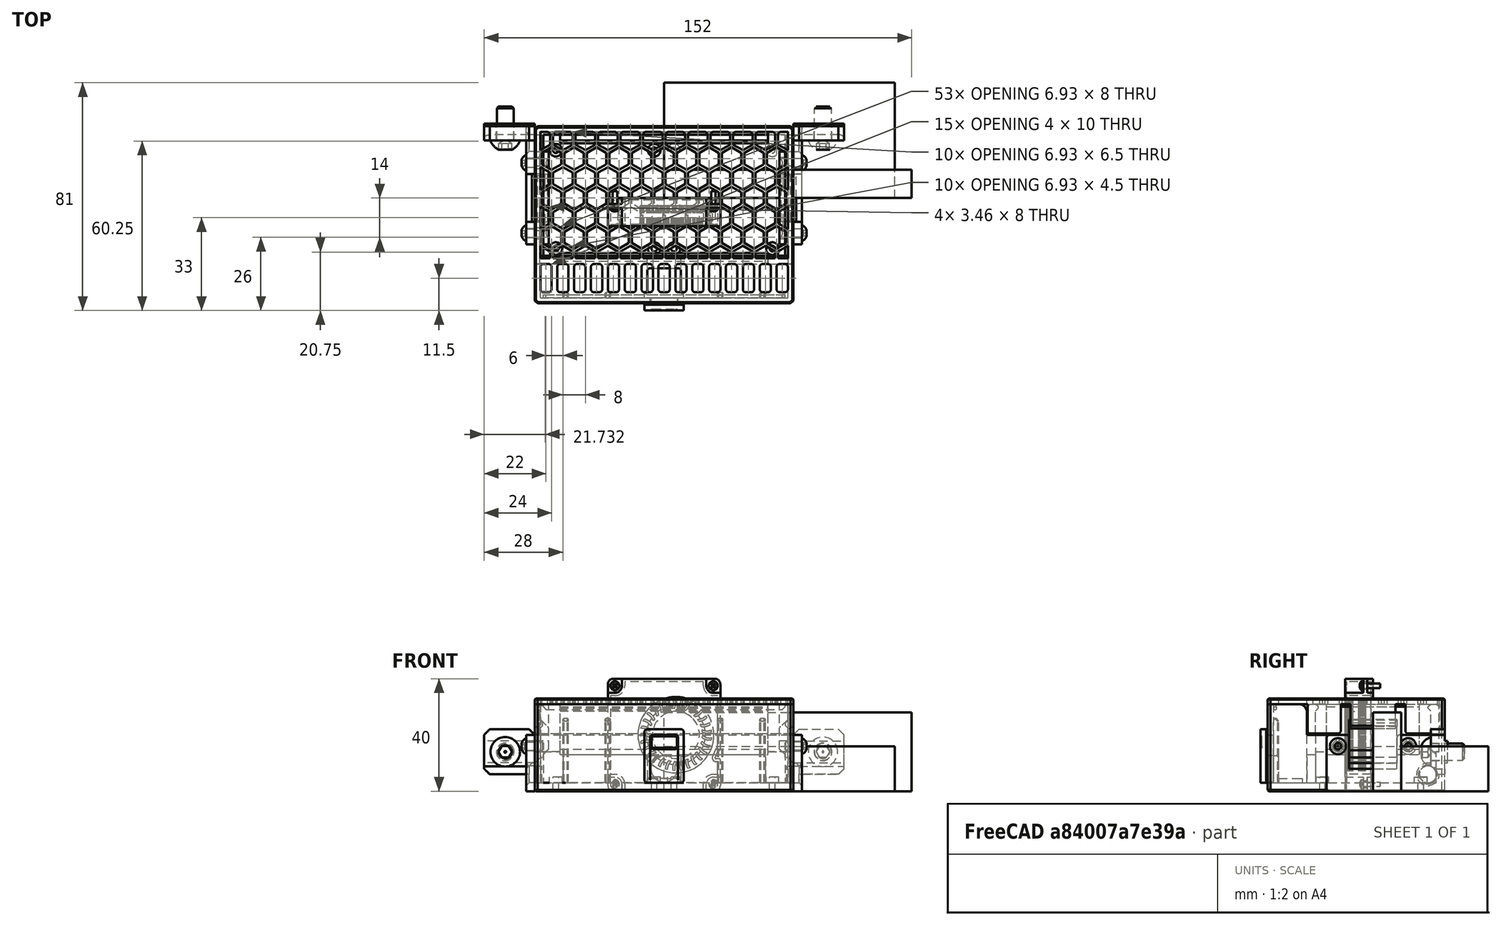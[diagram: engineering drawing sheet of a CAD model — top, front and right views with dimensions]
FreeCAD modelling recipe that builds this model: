
FCSTD DOCUMENT  (FreeCAD 0.19R24291 (Git))
Label: air-filter-assembly-A4
License: Other
LicenseURL: GPL3
objects: PartDesign::CoordinateSystem×17, Part::FeaturePython×10, App::Link×9, Part::Feature×6, App::Part×6, PartDesign::FeatureBase×4, PartDesign::Body×4, Part::Box×2, App::DocumentObjectGroup×2, App::FeaturePython×1
note: 43 computed .brp shape members not serialized (recipe doc carries the construction recipe); baked Part::Feature solids carry a one-line shape summary decoded from their .brp

FEATURE [Part::Box] Box  label="hepa-filter"
  AttacherType = Attacher::AttachEngine3D
  Height = 16
  Length = 82
  Placement = pos=(-41,-20.5,13) rot=(0,0,1;0rad)
  Width = 41
FEATURE [Part::Box] Box001  label="active-carbon-foam"
  AttacherType = Attacher::AttachEngine3D
  Height = 28
  Length = 88
  Placement = pos=(-44,-33.5,3) rot=(0,0,1;0rad)
  Width = 10
FEATURE [Part::Feature] Part__Mirroring001001  label="Chamfer010015011016001 (Mirror #1)002"
  shape: bbox 18 x 43 x 22 mm, 33 faces (baked)
FEATURE [Part::Feature] Chamfer010015011016002001
  shape: bbox 18 x 43 x 22 mm, 33 faces (baked)
FEATURE [Part::Feature] Chamfer010015011013001001
  shape: bbox 92 x 63 x 12.5 mm, 653 faces (baked)
FEATURE [Part::Feature] Chamfer010015011010001001
  shape: bbox 92 x 63 x 31 mm, 194 faces (baked)
FEATURE [Part::Feature] Cut019003010005001002001001  label="level002"
  shape: bbox 14 x 15 x 19 mm, 37 faces (baked)
FEATURE [Part::Feature] Fusion036012039009  label="4010-fan001"
  Placement = pos=(-21.1,-20.5,3) rot=(-1,0,0;1.5708rad)
  shape: bbox 40 x 40 x 10 mm, 256 faces, 2 solids (baked)
FEATURE [Part::FeaturePython] Screw  label="M3x6-Screw"  # Fasteners workbench fastener (typed FeaturePython)
  Placement = pos=(-49,12.5,16) rot=(0,-1,0;1.5708rad)
  baseObject = -> Part__Mirroring001001 [Edge89]
  diameter = 1
  invert = true
  length = 0
  lengthCustom = 6
  matchOuter = true
  offset = 0
  thread = false
  type = 39
FEATURE [Part::FeaturePython] Screw001  label="M3x6-Screw004"  # Fasteners workbench fastener (typed FeaturePython)
  Placement = pos=(-49,-12.5,16) rot=(0,-1,0;1.5708rad)
  baseObject = -> Part__Mirroring001001 [Edge91]
  diameter = 1
  invert = true
  length = 0
  lengthCustom = 6
  matchOuter = true
  offset = 0
  thread = false
  type = 39
FEATURE [Part::FeaturePython] Screw002  label="M3x6-Screw002"  # Fasteners workbench fastener (typed FeaturePython)
  Placement = pos=(49,12.5,16) rot=(0,1,0;1.5708rad)
  baseObject = -> Chamfer010015011016002001 [Edge89]
  diameter = 1
  invert = false
  length = 0
  lengthCustom = 6
  matchOuter = true
  offset = 0
  thread = false
  type = 39
FEATURE [Part::FeaturePython] Screw003  label="M3x6-Screw003"  # Fasteners workbench fastener (typed FeaturePython)
  Placement = pos=(49,-12.5,16) rot=(0,1,0;1.5708rad)
  baseObject = -> Chamfer010015011016002001 [Edge91]
  diameter = 1
  invert = false
  length = 0
  lengthCustom = 6
  matchOuter = true
  offset = 0
  thread = false
  type = 39
FEATURE [Part::FeaturePython] Screw004  label="M6x12-Screw"  # Fasteners workbench fastener (typed FeaturePython)
  Placement = pos=(-56.5,20.5,14) rot=(1,0,0;1.5708rad)
  baseObject = -> Part__Mirroring001001 [Edge57]
  diameter = 4
  invert = false
  length = 1
  lengthCustom = 12
  matchOuter = true
  offset = 0
  thread = false
  type = 39
FEATURE [Part::FeaturePython] Screw005  label="M6x12-Screw001"  # Fasteners workbench fastener (typed FeaturePython)
  Placement = pos=(56.5,20.5,14) rot=(1,0,0;1.5708rad)
  baseObject = -> Chamfer010015011016002001 [Edge40]
  diameter = 4
  invert = true
  length = 1
  lengthCustom = 12
  matchOuter = true
  offset = 0
  thread = false
  type = 39
FEATURE [PartDesign::CoordinateSystem] LCS_Origin
  AttacherType = Attacher::AttachEngine3D
  MapMode = 2
  Support = -> [X_Axis]
FEATURE [App::DocumentObjectGroup] Constraints
FEATURE [App::FeaturePython] Variables  # WARN: FeaturePython — macro-defined, semantics opaque (R4)
FEATURE [PartDesign::CoordinateSystem] LCS_0001  label="LCS_Base"
  AttacherType = Attacher::AttachEngine3D
  MapMode = 2
  Support = -> [X_Axis003]
FEATURE [PartDesign::FeatureBase] BaseFeature
  BaseFeature = -> Chamfer010015011010001001
FEATURE [PartDesign::CoordinateSystem] Local_CS  label="Local_CS_LFBH"
  AttacherType = Attacher::AttachEngine3D
  MapMode = 11
  Placement = pos=(-38.5,17,5) rot=(0,0,1;1.5708rad)
  Support = -> [BaseFeature]
FEATURE [PartDesign::CoordinateSystem] Local_CS001  label="Local_CS001_RFBH"
  AttacherType = Attacher::AttachEngine3D
  MapMode = 11
  Placement = pos=(3.5,17,5) rot=(0,0,1;1.5708rad)
  Support = -> [BaseFeature]
FEATURE [PartDesign::CoordinateSystem] Local_CS002  label="Local_CS002_LMBH"
  AttacherType = Attacher::AttachEngine3D
  MapMode = 11
  Placement = pos=(-46,-12.5,16) rot=(0.57735,0.57735,0.57735;2.0944rad)
  Support = -> [BaseFeature]
FEATURE [PartDesign::CoordinateSystem] Local_CS003  label="Local_CS003_RMBH"
  AttacherType = Attacher::AttachEngine3D
  MapMode = 11
  Placement = pos=(46,-12.5,16) rot=(0.57735,0.57735,0.57735;2.0944rad)
  Support = -> [BaseFeature]
FEATURE [PartDesign::CoordinateSystem] LCS_0
  AttacherType = Attacher::AttachEngine3D
  MapMode = 2
  Support = -> [X_Axis004]
FEATURE [PartDesign::FeatureBase] BaseFeature001
  BaseFeature = -> Fusion036012039009
FEATURE [PartDesign::CoordinateSystem] Local_CS004
  AttacherType = Attacher::AttachEngine3D
  MapMode = 11
  Placement = pos=(-17.5016,-2.099,37.4954) rot=(0.57735,0.57735,0.57735;4.18879rad)
  Support = -> [BaseFeature001]
FEATURE [PartDesign::Body] _010Fan  label="4010Fan"
  BaseFeature = -> Fusion036012039009
  Group = -> [BaseFeature001,LCS_0,Local_CS004]
  Origin = -> Origin004
  Tip = -> BaseFeature001
FEATURE [App::Link] AirFilterHousing001
  AssemblyType = Asm4EE
  AttachedBy = #LCS_0001
  AttachedTo = Parent Assembly#LCS_Origin
  LinkedObject = -> AirFilterHousing
  expr: Placement = LCS_Origin.Placement * AttachmentOffset * LCS_0001.Placement ^ -1
FEATURE [PartDesign::FeatureBase] BaseFeature002
  BaseFeature = -> Box
FEATURE [PartDesign::CoordinateSystem] Local_CS005
  AttacherType = Attacher::AttachEngine3D
  MapMode = 45
  Placement = pos=(41,41,16) rot=(0.57735,0.57735,0.57735;2.0944rad)
  Support = -> [BaseFeature002]
FEATURE [PartDesign::Body] HepaFilter
  BaseFeature = -> Box
  Group = -> [BaseFeature002,Local_CS005]
  Origin = -> Origin005
  Tip = -> BaseFeature002
FEATURE [PartDesign::CoordinateSystem] Local_CS006
  AttacherType = Attacher::AttachEngine3D
  MapMode = 45
  Placement = pos=(0,20.5,28.5) rot=(0.57735,0.57735,0.57735;2.0944rad)
  Support = -> [BaseFeature]
FEATURE [PartDesign::Body] AirFilterHousing
  BaseFeature = -> Chamfer010015011010001001
  Group = -> [BaseFeature,LCS_0001,Local_CS,Local_CS001,Local_CS002,Local_CS003,Local_CS006]
  Origin = -> Origin003
  Tip = -> BaseFeature
FEATURE [App::Link] HepaFilter001
  AssemblyType = Asm4EE
  AttachedBy = #Local_CS005
  AttachedTo = AirFilterHousing001#Local_CS006
  AttachmentOffset = pos=(0,0.5,0) rot=(0,0,1;0rad)
  LinkPlacement = pos=(-41,-20.5,13) rot=(0,0,1;0rad)
  LinkedObject = -> HepaFilter
  Placement = pos=(-41,-20.5,13) rot=(0,0,1;0rad)
  expr: Placement = AirFilterHousing001.Placement * Local_CS006.Placement * AttachmentOffset * Local_CS005.Placement ^ -1
FEATURE [PartDesign::CoordinateSystem] LCS_0002
  AttacherType = Attacher::AttachEngine3D
  MapMode = 2
  Support = -> [X_Axis006]
FEATURE [PartDesign::FeatureBase] BaseFeature003
  BaseFeature = -> Box001
FEATURE [PartDesign::CoordinateSystem] Local_CS007
  AttacherType = Attacher::AttachEngine3D
  MapMode = 45
  Placement = pos=(44,10,14) rot=(0.57735,0.57735,0.57735;4.18879rad)
  Support = -> [BaseFeature003]
FEATURE [PartDesign::Body] ActiveCarbonFoamCartridge
  BaseFeature = -> Box001
  Group = -> [BaseFeature003,LCS_0002,Local_CS007]
  Origin = -> Origin006
  Tip = -> BaseFeature003
FEATURE [App::Link] ActiveCarbonFoamCartridge001
  AssemblyType = Asm4EE
  AttachedBy = #Local_CS007
  AttachedTo = AirFilterHousing001#LCS_0001
  AttachmentOffset = pos=(0,-33.5,17) rot=(0.57735,-0.57735,0.57735;2.0944rad)
  LinkPlacement = pos=(44,-23.5,3) rot=(0,0,1;3.14159rad)
  LinkedObject = -> ActiveCarbonFoamCartridge
  Placement = pos=(44,-23.5,3) rot=(0,0,1;3.14159rad)
  expr: Placement = AirFilterHousing001.Placement * LCS_0001.Placement * AttachmentOffset * Local_CS007.Placement ^ -1
FEATURE [PartDesign::CoordinateSystem] LCS_0003
  AttacherType = Attacher::AttachEngine3D
  MapMode = 11
  Placement = pos=(46,-12.5,16) rot=(0.57735,0.57735,0.57735;2.0944rad)
  Support = -> [Chamfer010015011016002001]
FEATURE [App::Part] MountBracket_Right
  Group = -> [LCS_0003,Chamfer010015011016002001,Screw002,Screw005,Screw003]
  Origin = -> Origin007
FEATURE [App::Link] MountBracket_Right001
  AssemblyType = Asm4EE
  AttachedBy = #LCS_0003
  AttachedTo = AirFilterHousing001#Local_CS003
  LinkPlacement = pos=(-7.1e-15,5.3e-15,-7.1e-15) rot=(0,0,1;0rad)
  LinkedObject = -> MountBracket_Right
  Placement = pos=(-7.1e-15,5.3e-15,-7.1e-15) rot=(0,0,1;0rad)
  expr: Placement = AirFilterHousing001.Placement * Local_CS003.Placement * AttachmentOffset * LCS_0003.Placement ^ -1
FEATURE [PartDesign::CoordinateSystem] LCS_0004
  AttacherType = Attacher::AttachEngine3D
  MapMode = 11
  Placement = pos=(-46,-12.5,16) rot=(0.57735,0.57735,0.57735;2.0944rad)
  Support = -> [Part__Mirroring001001]
FEATURE [App::Part] MountBracket_Left
  Group = -> [LCS_0004,Part__Mirroring001001,Screw001,Screw004,Screw]
  Origin = -> Origin008
FEATURE [PartDesign::CoordinateSystem] LCS_0005
  AttacherType = Attacher::AttachEngine3D
  MapMode = 11
  Placement = pos=(-17.5016,-2.099,37.4954) rot=(0.57735,0.57735,0.57735;4.18879rad)
  Support = -> [BaseFeature001]
FEATURE [Part::FeaturePython] Screw006  label="M1.6x6-Screw"  # Fasteners workbench fastener (typed FeaturePython)
  Placement = pos=(17.4984,-3.499,2.49535) rot=(1,0,0;1.5708rad)
  baseObject = -> _010Fan [Edge196]
  diameter = 1
  invert = true
  length = 9
  lengthCustom = 6
  matchOuter = false
  offset = 0
  thread = false
  type = 35
FEATURE [Part::FeaturePython] Screw007  label="M1.6x6-Screw001"  # Fasteners workbench fastener (typed FeaturePython)
  Placement = pos=(-17.5016,-3.499,2.49535) rot=(1,0,0;1.5708rad)
  baseObject = -> _010Fan [Edge1]
  diameter = 1
  invert = true
  length = 9
  lengthCustom = 6
  matchOuter = false
  offset = 0
  thread = false
  type = 35
FEATURE [Part::FeaturePython] Screw008  label="M1.6x6-Screw002"  # Fasteners workbench fastener (typed FeaturePython)
  Placement = pos=(17.4984,-3.499,37.4954) rot=(1,0,0;1.5708rad)
  baseObject = -> _010Fan [Edge4]
  diameter = 1
  invert = true
  length = 9
  lengthCustom = 6
  matchOuter = false
  offset = 0
  thread = false
  type = 35
FEATURE [Part::FeaturePython] Screw009  label="M1.6x6-Screw003"  # Fasteners workbench fastener (typed FeaturePython)
  Placement = pos=(-17.5016,-3.499,37.4954) rot=(1,0,0;1.5708rad)
  baseObject = -> _010Fan [Edge190]
  diameter = 1
  invert = true
  length = 9
  lengthCustom = 6
  matchOuter = false
  offset = 0
  thread = false
  type = 35
FEATURE [App::Part] _010Fan001  label="4010Fan_"
  Group = -> [LCS_0005,Fusion036012039009,_010Fan,Screw006,Screw007,Screw008,Screw009]
  Origin = -> Origin009
FEATURE [App::Link] _010Fan_  label="4010Fan_001"
  AssemblyType = Asm4EE
  AttachedBy = #LCS_0005
  AttachedTo = AirFilterHousing001#Local_CS001
  AttachmentOffset = pos=(0,0,0) rot=(-1,0,0;3.14159rad)
  LinkPlacement = pos=(21.0016,-20.4954,2.901) rot=(-1,0,0;1.5708rad)
  LinkedObject = -> _010Fan001
  Placement = pos=(21.0016,-20.4954,2.901) rot=(-1,0,0;1.5708rad)
  expr: Placement = AirFilterHousing001.Placement * Local_CS001.Placement * AttachmentOffset * LCS_0005.Placement ^ -1
FEATURE [App::Link] _010Fan_001  label="4010Fan_002"
  AssemblyType = Asm4EE
  AttachedBy = #LCS_0005
  AttachedTo = AirFilterHousing001#Local_CS
  AttachmentOffset = pos=(0,0,0) rot=(1,0,0;3.14159rad)
  LinkPlacement = pos=(-20.9984,-20.4954,2.901) rot=(1,0,0;4.71239rad)
  LinkedObject = -> _010Fan001
  Placement = pos=(-20.9984,-20.4954,2.901) rot=(1,0,0;4.71239rad)
  expr: Placement = AirFilterHousing001.Placement * Local_CS.Placement * AttachmentOffset * LCS_0005.Placement ^ -1
FEATURE [PartDesign::CoordinateSystem] LCS_0006
  AttacherType = Attacher::AttachEngine3D
  MapMode = 2
  Support = -> [X_Axis010]
FEATURE [App::Part] FilterGrill
  Group = -> [LCS_0006,Chamfer010015011013001001]
  Origin = -> Origin010
FEATURE [App::Link] FilterGrill001
  AssemblyType = Asm4EE
  AttachedBy = #LCS_0006
  AttachedTo = AirFilterHousing001#LCS_0001
  LinkedObject = -> FilterGrill
  expr: Placement = AirFilterHousing001.Placement * LCS_0001.Placement * AttachmentOffset * LCS_0006.Placement ^ -1
FEATURE [App::Link] MountBracket_Left001
  AssemblyType = Asm4EE
  AttachedBy = #LCS_0004
  AttachedTo = AirFilterHousing001#Local_CS002
  LinkPlacement = pos=(0,0,-1.6e-14) rot=(0,0,1;0rad)
  LinkedObject = -> MountBracket_Left
  Placement = pos=(0,0,-1.6e-14) rot=(0,0,1;0rad)
  expr: Placement = AirFilterHousing001.Placement * Local_CS002.Placement * AttachmentOffset * LCS_0004.Placement ^ -1
FEATURE [PartDesign::CoordinateSystem] LCS_0007
  AttacherType = Attacher::AttachEngine3D
  MapMode = 2
  Support = -> [X_Axis011]
FEATURE [App::Part] Level
  Group = -> [LCS_0007,Cut019003010005001002001001]
  Origin = -> Origin011
FEATURE [App::DocumentObjectGroup] Parts
  Group = -> [AirFilterHousing,HepaFilter,ActiveCarbonFoamCartridge,MountBracket_Right,MountBracket_Left,_010Fan001,Box001,Box,Chamfer010015011010001001,FilterGrill,Level]
FEATURE [App::Link] Level001
  AssemblyType = Asm4EE
  AttachedBy = #LCS_0007
  AttachedTo = AirFilterHousing001#LCS_0001
  LinkedObject = -> Level
  expr: Placement = AirFilterHousing001.Placement * LCS_0001.Placement * AttachmentOffset * LCS_0007.Placement ^ -1
FEATURE [App::Part] Model  label="AirFilterAssembly"
  Configuration = 0
  Group = -> [LCS_Origin,Constraints,Variables,AirFilterHousing001,HepaFilter001,ActiveCarbonFoamCartridge001,MountBracket_Right001,_010Fan_,_010Fan_001,FilterGrill001,MountBracket_Left001,Level001]
  Origin = -> Origin
  Type = Assembly4 Model
